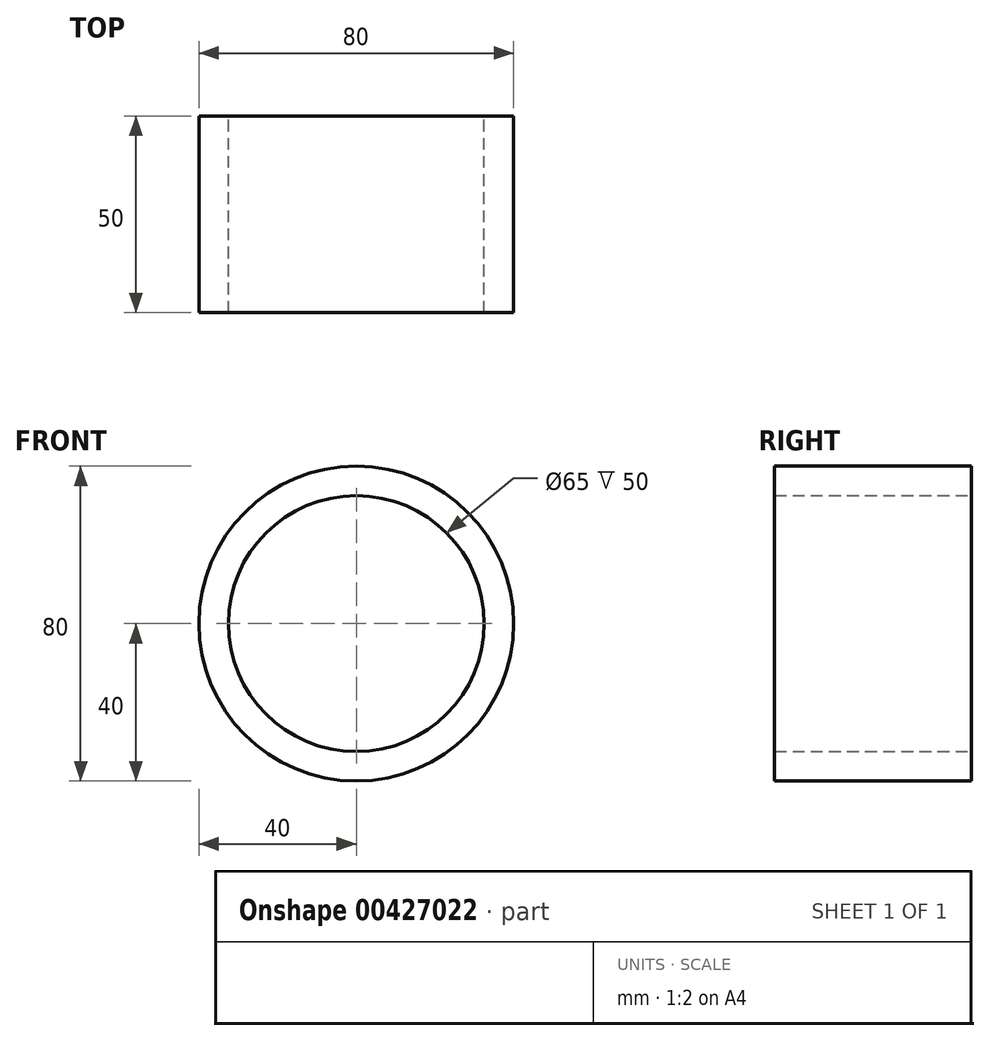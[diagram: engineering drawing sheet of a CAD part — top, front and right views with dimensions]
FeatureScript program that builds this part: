
annotation { "Feature Type Name" : "Feature", "Feature Type Description" : "" }
export const myFeature = defineFeature(function(context is Context, id is Id, definition is map)
    precondition{}
    {
        {
            var Q0;
            Q0=qCreatedBy(makeId("Front.planeOp"),FACE);
            var sketch = newSketch(context, id + "F0", { "sketchPlane" : qUnion([Q0])});
            skCircle(sketch, "E0", {"center": v(0, 0) * mm, "radius": 32.5 * mm});
            skCircle(sketch, "E1", {"center": v(0, 0) * mm, "radius": 40 * mm});
            skSolve(sketch);
        }
        {
            var Q0;
            Q0 = qSketchRegion(id + "F0", true);
            extrude(context, id + "F1", {"entities" : qUnion([Q0]), "endBound" : BoundingType.SYMMETRIC, "depth" : 50 * mm});
        }
    });
